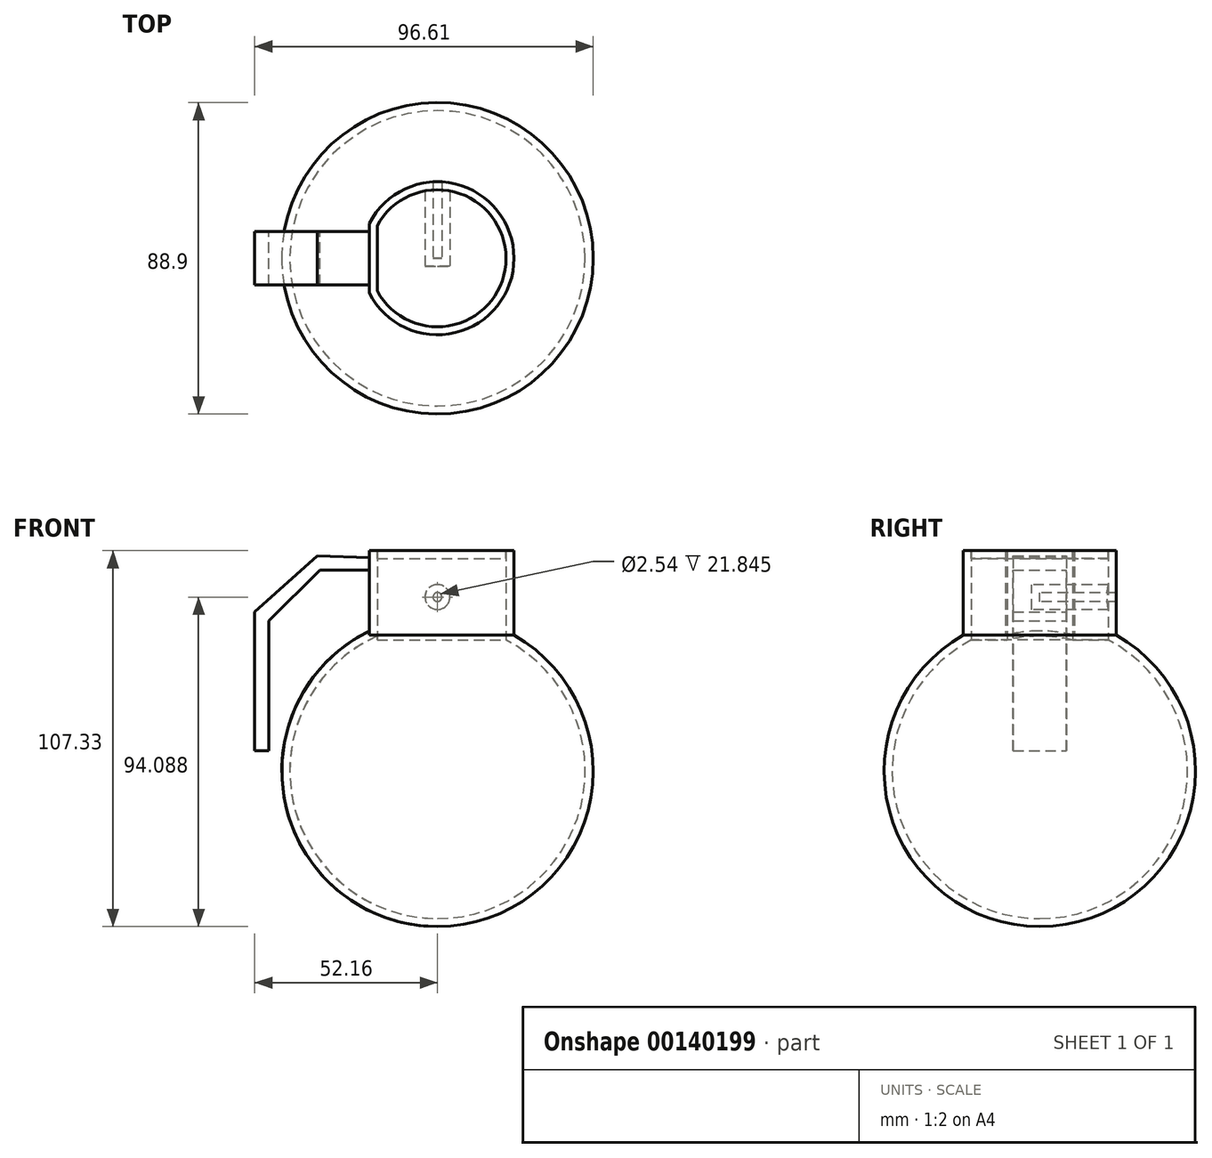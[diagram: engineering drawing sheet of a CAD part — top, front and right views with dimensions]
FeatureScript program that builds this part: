
annotation { "Feature Type Name" : "Feature", "Feature Type Description" : "" }
export const myFeature = defineFeature(function(context is Context, id is Id, definition is map)
    precondition{}
    {
        {
            var Q0;
            Q0=qCreatedBy(makeId("Front.planeOp"),FACE);
            var sketch = newSketch(context, id + "F0", { "sketchPlane" : qUnion([Q0])});
            skArc(sketch, "E0", {"start": v(0, -44.45) * mm, "mid": v(44.45, 0) * mm, "end": v(0, 44.45) * mm});
            skLineSegment(sketch, "E1", {"start": v(0, 0) * mm, "end": v(0, 51.32) * mm, "construction": true});
            skLineSegment(sketch, "E2", {"start": v(0, 0) * mm, "end": v(0, -50.11) * mm, "construction": true});
            skLineSegment(sketch, "E3", {"start": v(0, 44.45) * mm, "end": v(0, -44.45) * mm});
            skSolve(sketch);
        }
        {
            var Q0;
            Q0 = qSketchRegion(id + "F0", true);
            var Q1;
            Q1=sQuery(id+"F0.wireOp",EDGE,"E1");
            revolve(context, id + "F1", {"entities" : qUnion([Q0]), "axis" : qUnion([Q1]), "revolveType" : RevolveType.FULL});
        }
        {
            var Q0;
            Q0=qCreatedBy(makeId("Front.planeOp"),FACE);
            var sketch = newSketch(context, id + "F2", { "sketchPlane" : qUnion([Q0])});
            skLineSegment(sketch, "E4.bottom", {"start": v(39.97, 61.67) * mm, "end": v(-54.13, 61.67) * mm});
            skLineSegment(sketch, "E4.top", {"start": v(39.97, 38.73) * mm, "end": v(-54.13, 38.73) * mm});
            skLineSegment(sketch, "E4.left", {"start": v(39.97, 61.67) * mm, "end": v(39.97, 38.73) * mm});
            skLineSegment(sketch, "E4.right", {"start": v(-54.13, 61.67) * mm, "end": v(-54.13, 38.73) * mm});
            skSolve(sketch);
        }
        {
            var Q0;
            Q0 = qSketchRegion(id + "F2", true);
            extrude(context, id + "F3", {"entities" : qUnion([Q0]), "operationType" : NewBodyOperationType.REMOVE, "endBound" : BoundingType.THROUGH_ALL, "oppositeDirection" : true, "depth" : 25.4 * mm, "hasSecondDirection" : true, "secondDirectionBound" : SecondDirectionBoundingType.THROUGH_ALL, "secondDirectionOppositeDirection" : false, "secondDirectionDepth" : 25.4 * mm});
        }
        {
            var Q0;
            Q0=makeQuery(id+"F3.boolean.opBoolean","COPY",FACE,{"derivedFrom":makeQuery(id+"F3.opExtrude","SWEPT_FACE",FACE,{"disambiguationData":[OSD([sQuery(id+"F2.wireOp",EDGE,"E4.top")])]})});
            var sketch = newSketch(context, id + "F4", { "sketchPlane" : qUnion([Q0])});
            skLineSegment(sketch, "E5.bottom", {"start": v(11.76, -18.38) * mm, "end": v(-11.34, -18.38) * mm});
            skLineSegment(sketch, "E5.top", {"start": v(11.76, 16.27) * mm, "end": v(-11.34, 16.27) * mm});
            skLineSegment(sketch, "E5.left", {"start": v(11.76, -18.38) * mm, "end": v(11.76, 16.27) * mm});
            skLineSegment(sketch, "E5.right", {"start": v(-11.34, -18.38) * mm, "end": v(-11.34, 16.27) * mm});
            skSolve(sketch);
        }
        {
            var Q0;
            Q0=makeQuery(id+"F4.imprint","IMPRINT",FACE,{"disambiguationData":[TD([[makeQuery(id+"F4.imprint","IMPRINT",EDGE,{"derivedFrom":sQuery(id+"F4.wireOp",EDGE,"E5.bottom")}),1.0]])]});
            var sketch = newSketch(context, id + "F5", { "sketchPlane" : qUnion([Q0])});
            skCircle(sketch, "E6", {"center": v(0, 0) * mm, "radius": 21.85 * mm});
            skSolve(sketch);
        }
        {
            var Q0;
            Q0 = qSketchRegion(id + "F5", true);
            extrude(context, id + "F6", {"entities" : qUnion([Q0]), "operationType" : NewBodyOperationType.ADD, "depth" : 24.15 * mm});
        }
        {
            var Q0;
            Q0=makeQuery(id+"F6.opExtrude","CAP_FACE",FACE,{"disambiguationData":[OSD([sQuery(id+"F5.wireOp",EDGE,"E6")])],"isStart":false});
            var sketch = newSketch(context, id + "F7", { "sketchPlane" : qUnion([Q0])});
            skLineSegment(sketch, "E7.bottom", {"start": v(-19.49, 16.21) * mm, "end": v(-29.01, 16.21) * mm});
            skLineSegment(sketch, "E7.top", {"start": v(-19.49, -18.29) * mm, "end": v(-29.01, -18.29) * mm});
            skLineSegment(sketch, "E7.left", {"start": v(-19.49, 16.21) * mm, "end": v(-19.49, -18.29) * mm});
            skLineSegment(sketch, "E7.right", {"start": v(-29.01, 16.21) * mm, "end": v(-29.01, -18.29) * mm});
            skSolve(sketch);
        }
        {
            var Q0;
            Q0 = qSketchRegion(id + "F7", true);
            var Q1;
            Q1=makeQuery(id+"F1.opRevolve","SWEPT_FACE",FACE,{"disambiguationData":[OSD([sQuery(id+"F0.wireOp",EDGE,"E0")])]});
            extrude(context, id + "F8", {"entities" : qUnion([Q0]), "operationType" : NewBodyOperationType.REMOVE, "endBound" : BoundingType.UP_TO_SURFACE, "oppositeDirection" : true, "endBoundEntityFace" : qUnion([Q1]), "depth" : 25.4 * mm});
        }
        {
            var Q0;
            Q0=qCreatedBy(makeId("Front.planeOp"),FACE);
            var sketch = newSketch(context, id + "F9", { "sketchPlane" : qUnion([Q0])});
            skLineSegment(sketch, "E8", {"start": v(-19.49, 60.85) * mm, "end": v(-19.49, 52.66) * mm});
            skLineSegment(sketch, "E9", {"start": v(-19.49, 60.85) * mm, "end": v(-34.26, 61.37) * mm});
            skLineSegment(sketch, "E10", {"start": v(-34.26, 61.37) * mm, "end": v(-52.16, 45.43) * mm});
            skLineSegment(sketch, "E11", {"start": v(-52.16, 45.43) * mm, "end": v(-52.16, 5.79) * mm});
            skLineSegment(sketch, "E12", {"start": v(-52.16, 5.79) * mm, "end": v(-48.2, 5.79) * mm});
            skLineSegment(sketch, "E13", {"start": v(-48.2, 5.79) * mm, "end": v(-48.2, 42.87) * mm});
            skLineSegment(sketch, "E14", {"start": v(-48.2, 42.87) * mm, "end": v(-33.5, 57.33) * mm});
            skLineSegment(sketch, "E15", {"start": v(-33.5, 57.33) * mm, "end": v(-19.49, 57.33) * mm});
            skPoint(sketch, "E15.endSnap0", {"position": v(-19.49, 56.76) * mm});
            skSolve(sketch);
        }
        {
            var Q0;
            Q0 = qSketchRegion(id + "F9", true);
            extrude(context, id + "F10", {"entities" : qUnion([Q0]), "operationType" : NewBodyOperationType.ADD, "endBound" : BoundingType.SYMMETRIC, "depth" : 15.24 * mm});
        }
        {
            var Q0;
            Q0=qCreatedBy(makeId("Front.planeOp"),FACE);
            var sketch = newSketch(context, id + "F11", { "sketchPlane" : qUnion([Q0])});
            skCircle(sketch, "E16", {"center": v(0, 49.64) * mm, "radius": 1.27 * mm});
            skSolve(sketch);
        }
        {
            var Q0;
            Q0 = qSketchRegion(id + "F11", true);
            extrude(context, id + "F12", {"entities" : qUnion([Q0]), "operationType" : NewBodyOperationType.REMOVE, "endBound" : BoundingType.THROUGH_ALL, "oppositeDirection" : true, "depth" : 25.4 * mm});
        }
        {
            var Q0;
            Q0=makeQuery(id+"F6.opExtrude","CAP_FACE",FACE,{"disambiguationData":[OSD([sQuery(id+"F5.wireOp",EDGE,"E6")])],"isStart":false});
            shell(context, id + "F13", {"entities" : qUnion([Q0]), "thickness" : 2.3 * mm});
        }
        {
            var Q0;
            {var subQ0=sQuery(id+"F5.wireOp",EDGE,"E6");Q0=makeQuery(id+"F13.opShell","OFFSET_FACE",FACE,{"disambiguationData":[OSD([subQ0]),TDD([makeQuery(id+"F6.opExtrude","CAP_FACE",FACE,{"disambiguationData":[OSD([subQ0])],"isStart":true})])]});}
            var sketch = newSketch(context, id + "F14", { "sketchPlane" : qUnion([Q0])});
            skArc(sketch, "E17.0", {"start": v(-17.2, -9.3) * mm, "mid": v(19.56, 0) * mm, "end": v(-17.2, 9.3) * mm});
            skLineSegment(sketch, "E18.0", {"start": v(-17.2, 9.3) * mm, "end": v(-17.2, -9.3) * mm});
            skSolve(sketch);
        }
        {
            var Q0;
            Q0 = qSketchRegion(id + "F14", true);
            extrude(context, id + "F15", {"entities" : qUnion([Q0]), "operationType" : NewBodyOperationType.REMOVE, "oppositeDirection" : true, "depth" : 25.4 * mm});
        }
        {
            var Q0;
            Q0=makeQuery(id+"F6.opExtrude","CAP_FACE",FACE,{"disambiguationData":[OSD([sQuery(id+"F5.wireOp",EDGE,"E6")])],"isStart":false});
            var sketch = newSketch(context, id + "F16", { "sketchPlane" : qUnion([Q0])});
            skArc(sketch, "E19.0", {"start": v(-17.2, -9.3) * mm, "mid": v(19.56, 0) * mm, "end": v(-17.2, 9.3) * mm});
            skLineSegment(sketch, "E20.0", {"start": v(-17.2, 9.3) * mm, "end": v(-17.2, -9.3) * mm});
            skSolve(sketch);
        }
        {
            var Q0;
            Q0 = qSketchRegion(id + "F16", true);
            extrude(context, id + "F17", {"entities" : qUnion([Q0]), "oppositeDirection" : true, "depth" : 2.3 * mm});
        }
    });
